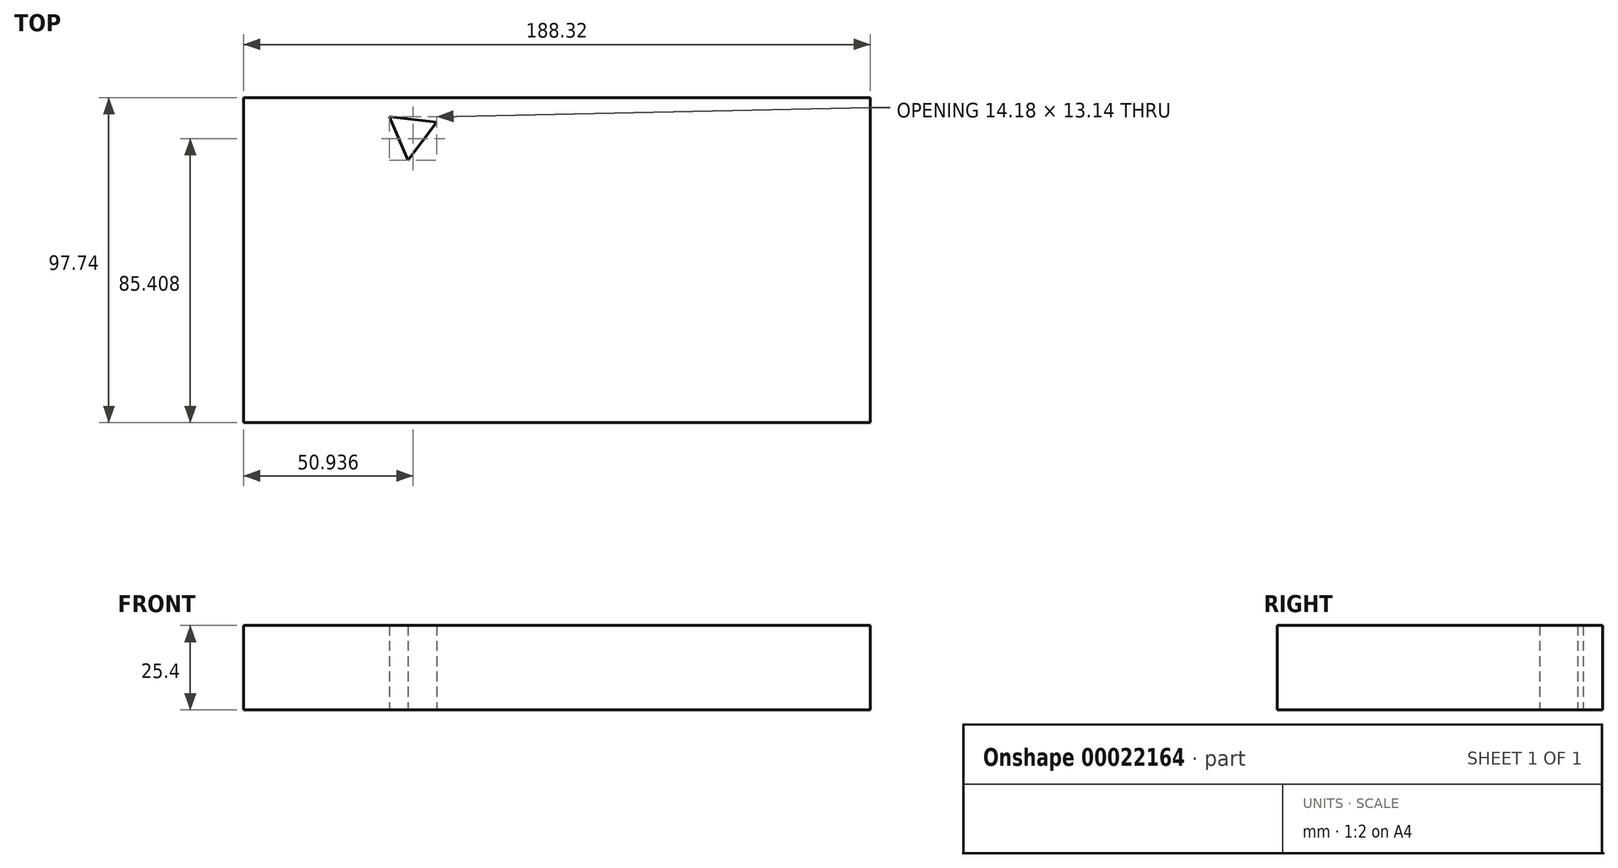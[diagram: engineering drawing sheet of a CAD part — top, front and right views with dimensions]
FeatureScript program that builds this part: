
annotation { "Feature Type Name" : "Feature", "Feature Type Description" : "" }
export const myFeature = defineFeature(function(context is Context, id is Id, definition is map)
    precondition{}
    {
        {
            var Q0;
            Q0=qCreatedBy(makeId("Top.planeOp"),FACE);
            var sketch = newSketch(context, id + "F0", { "sketchPlane" : qUnion([Q0])});
            skLineSegment(sketch, "E0.bottom", {"start": v(-94.16, 47.83) * mm, "end": v(94.16, 47.83) * mm});
            skLineSegment(sketch, "E0.top", {"start": v(-94.16, -49.91) * mm, "end": v(94.16, -49.91) * mm});
            skLineSegment(sketch, "E0.left", {"start": v(-94.16, 47.83) * mm, "end": v(-94.16, -49.91) * mm});
            skLineSegment(sketch, "E0.right", {"start": v(94.16, 47.83) * mm, "end": v(94.16, -49.91) * mm});
            skCircle(sketch, "E1.cCircle", {"center": v(-43.72, 37.12) * mm, "radius": 4.12 * mm, "construction": true});
            skLineSegment(sketch, "E1.0", {"start": v(-36.13, 40.36) * mm, "end": v(-44.7, 28.93) * mm});
            skLineSegment(sketch, "E1.1", {"start": v(-44.7, 28.93) * mm, "end": v(-50.32, 42.07) * mm});
            skLineSegment(sketch, "E1.2", {"start": v(-50.32, 42.07) * mm, "end": v(-36.13, 40.36) * mm});
            skPoint(sketch, "E1.0.midPoint", {"position": v(-40.42, 34.64) * mm});
            skSolve(sketch);
        }
        {
            var Q0;
            Q0=makeQuery(id+"F0.imprint","IMPRINT",FACE,{"disambiguationData":[TD([[makeQuery(id+"F0.imprint","IMPRINT",EDGE,{"derivedFrom":sQuery(id+"F0.wireOp",EDGE,"E0.bottom")}),-1.0]])]});
            extrude(context, id + "F1", {"entities" : qUnion([Q0]), "depth" : 25.4 * mm});
        }
    });
